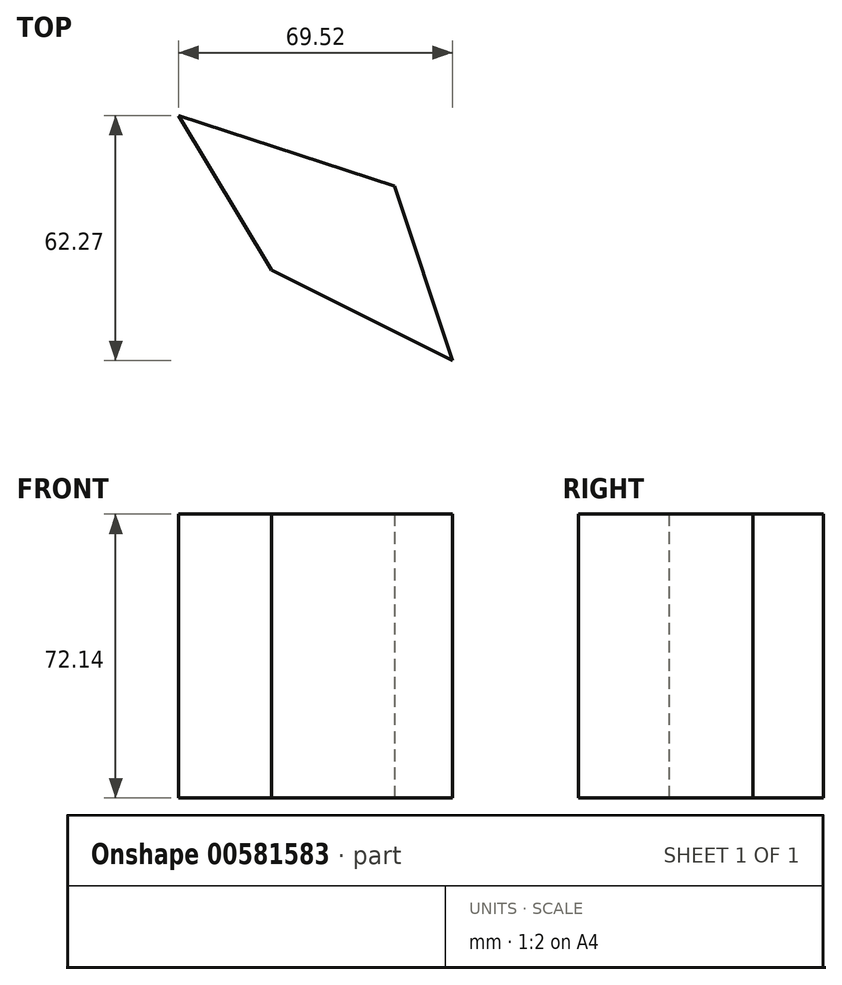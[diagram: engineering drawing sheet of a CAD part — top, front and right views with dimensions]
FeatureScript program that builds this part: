
annotation { "Feature Type Name" : "Feature", "Feature Type Description" : "" }
export const myFeature = defineFeature(function(context is Context, id is Id, definition is map)
    precondition{}
    {
        {
            var Q0;
            Q0=qCreatedBy(makeId("Top.planeOp"),FACE);
            var sketch = newSketch(context, id + "F0", { "sketchPlane" : qUnion([Q0])});
            skLineSegment(sketch, "E0", {"start": v(-43.54, -7.1) * mm, "end": v(-98.35, 10.79) * mm});
            skLineSegment(sketch, "E1", {"start": v(-98.35, 10.79) * mm, "end": v(-74.82, -28.5) * mm});
            skLineSegment(sketch, "E2", {"start": v(-74.82, -28.5) * mm, "end": v(-28.83, -51.48) * mm});
            skLineSegment(sketch, "E3", {"start": v(-43.54, -7.1) * mm, "end": v(-28.83, -51.48) * mm});
            skSolve(sketch);
        }
        {
            var Q0;
            Q0=makeQuery(id+"F0.imprint","IMPRINT",FACE,{"disambiguationData":[TD([[makeQuery(id+"F0.imprint","IMPRINT",EDGE,{"derivedFrom":sQuery(id+"F0.wireOp",EDGE,"E0")}),1.0]])]});
            extrude(context, id + "F1", {"entities" : qUnion([Q0]), "depth" : 72.14 * mm, "offsetDistance" : 25.4 * mm});
        }
    });
